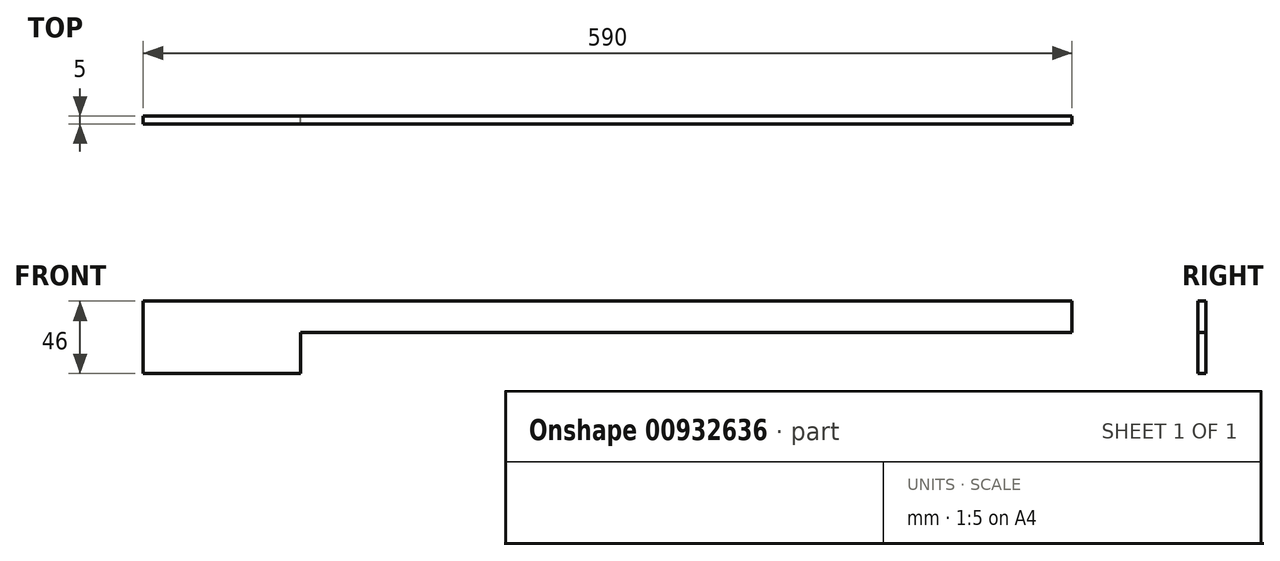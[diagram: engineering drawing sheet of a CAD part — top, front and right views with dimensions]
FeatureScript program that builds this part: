
annotation { "Feature Type Name" : "Feature", "Feature Type Description" : "" }
export const myFeature = defineFeature(function(context is Context, id is Id, definition is map)
    precondition{}
    {
        {
            var Q0;
            Q0=qCreatedBy(makeId("Front.planeOp"),FACE);
            var sketch = newSketch(context, id + "F0", { "sketchPlane" : qUnion([Q0])});
            skLineSegment(sketch, "E0", {"start": v(0, 0) * mm, "end": v(0, 46) * mm});
            skLineSegment(sketch, "E1", {"start": v(0, 46) * mm, "end": v(590, 46) * mm});
            skLineSegment(sketch, "E2", {"start": v(590, 46) * mm, "end": v(590, 26) * mm});
            skLineSegment(sketch, "E3", {"start": v(590, 26) * mm, "end": v(100, 26) * mm});
            skLineSegment(sketch, "E4", {"start": v(100, 26) * mm, "end": v(100, 0) * mm});
            skLineSegment(sketch, "E5", {"start": v(100, 0) * mm, "end": v(0, 0) * mm});
            skSolve(sketch);
        }
        {
            var Q0;
            Q0=makeQuery(id+"F0.imprint","IMPRINT",FACE,{"disambiguationData":[TD([[makeQuery(id+"F0.imprint","IMPRINT",EDGE,{"derivedFrom":sQuery(id+"F0.wireOp",EDGE,"E0")}),-1.0]])]});
            extrude(context, id + "F1", {"entities" : qUnion([Q0]), "depth" : 5 * mm, "offsetDistance" : 25 * mm});
        }
    });
